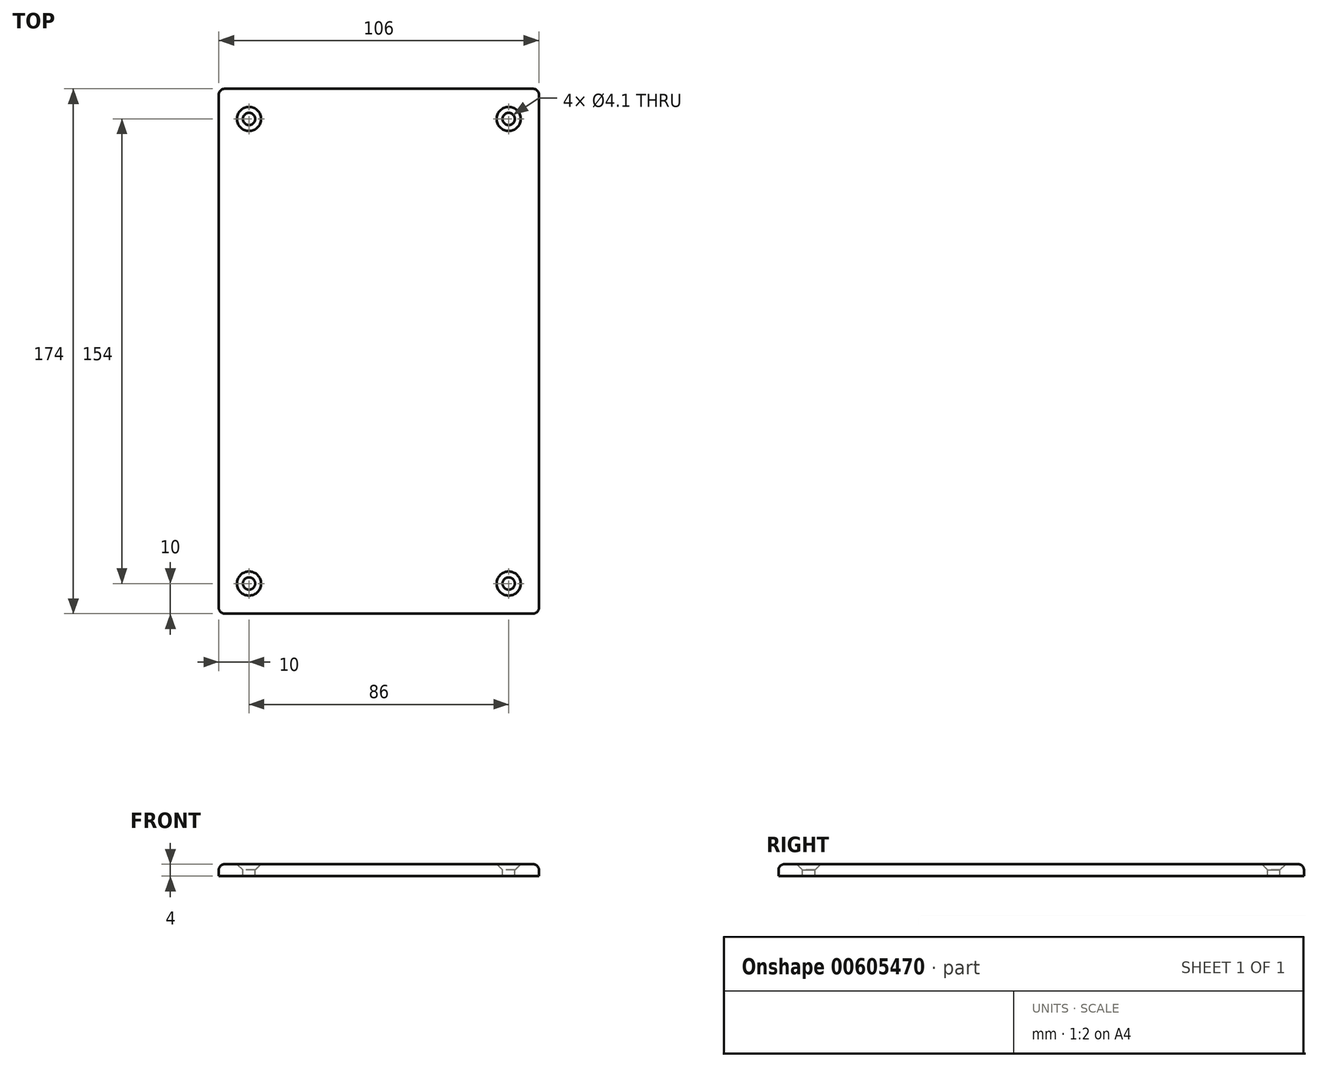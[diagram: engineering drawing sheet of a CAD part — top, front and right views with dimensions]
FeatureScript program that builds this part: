
annotation { "Feature Type Name" : "Feature", "Feature Type Description" : "" }
export const myFeature = defineFeature(function(context is Context, id is Id, definition is map)
    precondition{}
    {
        {
            var Q0;
            Q0=qCreatedBy(makeId("Top.planeOp"),FACE);
            var sketch = newSketch(context, id + "F0", { "sketchPlane" : qUnion([Q0])});
            skLineSegment(sketch, "E0.bottom", {"start": v(0, 0) * mm, "end": v(106, 0) * mm});
            skLineSegment(sketch, "E0.top", {"start": v(0, 174) * mm, "end": v(106, 174) * mm});
            skLineSegment(sketch, "E0.left", {"start": v(0, 0) * mm, "end": v(0, 174) * mm});
            skLineSegment(sketch, "E0.right", {"start": v(106, 0) * mm, "end": v(106, 174) * mm});
            skSolve(sketch);
        }
        {
            var Q0;
            Q0 = qSketchRegion(id + "F0", true);
            extrude(context, id + "F1", {"entities" : qUnion([Q0]), "depth" : 4 * mm, "offsetDistance" : 25 * mm});
        }
        {
            var Q0;
            Q0=makeQuery(id+"F1.opExtrude","CAP_EDGE",EDGE,{"disambiguationData":[OSD([sQuery(id+"F0.wireOp",EDGE,"E0.bottom")])],"isStart":false});
            var Q1;
            Q1=makeQuery(id+"F1.opExtrude","CAP_EDGE",EDGE,{"disambiguationData":[OSD([sQuery(id+"F0.wireOp",EDGE,"E0.left")])],"isStart":false});
            var Q2;
            Q2=makeQuery(id+"F1.opExtrude","CAP_EDGE",EDGE,{"disambiguationData":[OSD([sQuery(id+"F0.wireOp",EDGE,"E0.right")])],"isStart":false});
            var Q3;
            Q3=makeQuery(id+"F1.opExtrude","CAP_EDGE",EDGE,{"disambiguationData":[OSD([sQuery(id+"F0.wireOp",EDGE,"E0.top")])],"isStart":false});
            fillet(context, id + "F2", {"entities" : qUnion([Q0, Q1, Q2, Q3]), "radius" : 2 * mm, "tangentPropagation" : true, "allowEdgeOverflow" : false});
        }
        {
            var Q0;
            Q0=makeQuery(id+"F1.opExtrude","SWEPT_EDGE",EDGE,{"disambiguationData":[OSD([sQuery(id+"F0.wireOp",EDGE,"E0.bottom"),sQuery(id+"F0.wireOp",EDGE,"E0.right")])]});
            var Q1;
            Q1=makeQuery(id+"F1.opExtrude","SWEPT_EDGE",EDGE,{"disambiguationData":[OSD([sQuery(id+"F0.wireOp",EDGE,"E0.bottom"),sQuery(id+"F0.wireOp",EDGE,"E0.left")])]});
            var Q2;
            Q2=makeQuery(id+"F1.opExtrude","SWEPT_EDGE",EDGE,{"disambiguationData":[OSD([sQuery(id+"F0.wireOp",EDGE,"E0.top"),sQuery(id+"F0.wireOp",EDGE,"E0.left")])]});
            var Q3;
            Q3=makeQuery(id+"F1.opExtrude","SWEPT_EDGE",EDGE,{"disambiguationData":[OSD([sQuery(id+"F0.wireOp",EDGE,"E0.top"),sQuery(id+"F0.wireOp",EDGE,"E0.right")])]});
            fillet(context, id + "F3", {"entities" : qUnion([Q0, Q1, Q2, Q3]), "radius" : 2 * mm, "tangentPropagation" : true, "allowEdgeOverflow" : false});
        }
        {
            var Q0;
            Q0=makeQuery(id+"F1.opExtrude","CAP_FACE",FACE,{"disambiguationData":[OSD([sQuery(id+"F0.wireOp",EDGE,"E0.bottom"),sQuery(id+"F0.wireOp",EDGE,"E0.top"),sQuery(id+"F0.wireOp",EDGE,"E0.left"),sQuery(id+"F0.wireOp",EDGE,"E0.right")])],"isStart":false});
            var sketch = newSketch(context, id + "F4", { "sketchPlane" : qUnion([Q0])});
            skPoint(sketch, "E1", {"position": v(96, 164) * mm});
            skLineSegment(sketch, "E2.0", {"start": v(2, 174) * mm, "end": v(104, 174) * mm});
            skLineSegment(sketch, "E3.0", {"start": v(0, 2) * mm, "end": v(0, 172) * mm});
            skLineSegment(sketch, "E4.0", {"start": v(104, 0) * mm, "end": v(2, 0) * mm});
            skLineSegment(sketch, "E5.0", {"start": v(106, 172) * mm, "end": v(106, 2) * mm});
            skLineSegment(sketch, "E6", {"start": v(53, 174) * mm, "end": v(53, 0) * mm});
            skLineSegment(sketch, "E7", {"start": v(106, 87) * mm, "end": v(0, 87) * mm});
            skPoint(sketch, "E8.MirrorP", {"position": v(10, 164) * mm});
            skPoint(sketch, "E9.MirrorP", {"position": v(10, 10) * mm});
            skPoint(sketch, "E10.MirrorP", {"position": v(96, 10) * mm});
            skSolve(sketch);
        }
        {
            var Q0;
            Q0=sQuery(id+"F4.wireOp",VERTEX,"E8.MirrorP");
            var Q1;
            Q1=sQuery(id+"F4.wireOp",VERTEX,"E9.MirrorP");
            var Q2;
            Q2=sQuery(id+"F4.wireOp",VERTEX,"E1");
            var Q3;
            Q3=sQuery(id+"F4.wireOp",VERTEX,"E10.MirrorP");
            var Q4;
            Q4=makeQuery(id+"F1.opExtrude","SWEPT_BODY",BODY,{"disambiguationData":[OSD([sQuery(id+"F0.wireOp",EDGE,"E0.bottom"),sQuery(id+"F0.wireOp",EDGE,"E0.top"),sQuery(id+"F0.wireOp",EDGE,"E0.left"),sQuery(id+"F0.wireOp",EDGE,"E0.right")])]});
            hole(context, id + "F5", {"style" : HoleStyle.C_SINK, "endStyle" : HoleEndStyle.BLIND, "holeDiameter" : 4.1 * mm, "cSinkDiameter" : 8 * mm, "cSinkAngle" : 90 * degree, "majorDiameter" : 5 * mm, "holeDepth" : 40 * mm, "isTappedThrough" : true, "tappedDepth" : 12 * mm, "tapClearance" : 3, "locations" : qUnion([Q0, Q1, Q2, Q3]), "scope" : qUnion([Q4])});
        }
    });
